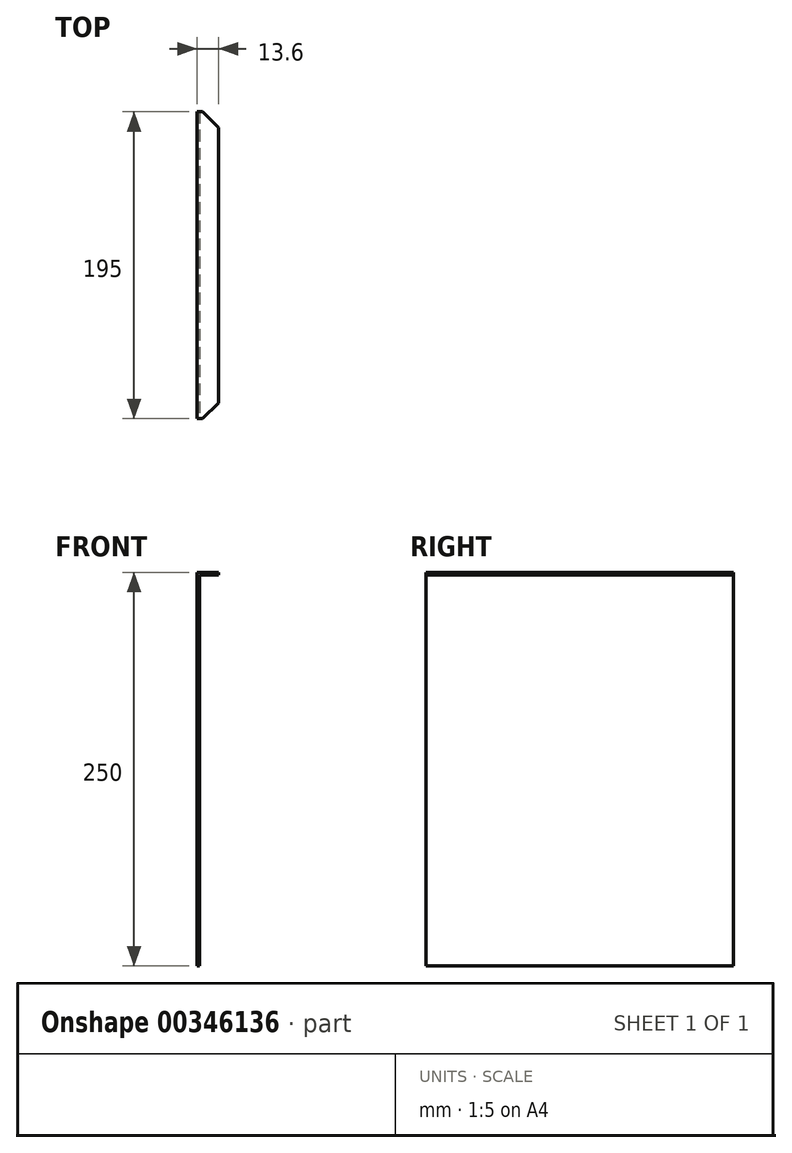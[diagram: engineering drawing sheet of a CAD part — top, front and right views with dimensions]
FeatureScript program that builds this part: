
annotation { "Feature Type Name" : "Feature", "Feature Type Description" : "" }
export const myFeature = defineFeature(function(context is Context, id is Id, definition is map)
    precondition{}
    {
        {
            var Q0;
            Q0=qCreatedBy(makeId("Right.planeOp"),FACE);
            var sketch = newSketch(context, id + "F0", { "sketchPlane" : qUnion([Q0])});
            skLineSegment(sketch, "E0.bottom", {"start": v(97.5, -125) * mm, "end": v(-97.5, -125) * mm});
            skLineSegment(sketch, "E0.top", {"start": v(97.5, 125) * mm, "end": v(-97.5, 125) * mm});
            skLineSegment(sketch, "E0.left", {"start": v(97.5, -125) * mm, "end": v(97.5, 125) * mm});
            skLineSegment(sketch, "E0.right", {"start": v(-97.5, -125) * mm, "end": v(-97.5, 125) * mm});
            skPoint(sketch, "E0.middle", {"position": v(0, 0) * mm});
            skSolve(sketch);
        }
        {
            var Q0;
            Q0=makeQuery(id+"F0.imprint","IMPRINT",FACE,{"disambiguationData":[TD([[makeQuery(id+"F0.imprint","IMPRINT",EDGE,{"derivedFrom":sQuery(id+"F0.wireOp",EDGE,"E0.bottom")}),-1.0]])]});
            extrude(context, id + "F1", {"entities" : qUnion([Q0]), "depth" : 1.6 * mm});
        }
        {
            var Q0;
            Q0=makeQuery(id+"F1.opExtrude","CAP_FACE",FACE,{"disambiguationData":[OSD([sQuery(id+"F0.wireOp",EDGE,"E0.bottom"),sQuery(id+"F0.wireOp",EDGE,"E0.top"),sQuery(id+"F0.wireOp",EDGE,"E0.left"),sQuery(id+"F0.wireOp",EDGE,"E0.right")])],"isStart":false});
            var sketch = newSketch(context, id + "F2", { "sketchPlane" : qUnion([Q0])});
            skLineSegment(sketch, "E1.bottom", {"start": v(97.5, 123.4) * mm, "end": v(-97.5, 123.4) * mm});
            skLineSegment(sketch, "E1.top", {"start": v(97.5, 125) * mm, "end": v(-97.5, 125) * mm});
            skLineSegment(sketch, "E1.left", {"start": v(97.5, 123.4) * mm, "end": v(97.5, 125) * mm});
            skLineSegment(sketch, "E1.right", {"start": v(-97.5, 123.4) * mm, "end": v(-97.5, 125) * mm});
            skPoint(sketch, "E1.middle", {"position": v(0, 124.2) * mm});
            skSolve(sketch);
        }
        {
            var Q0;
            Q0=makeQuery(id+"F2.imprint","IMPRINT",FACE,{"disambiguationData":[TD([[makeQuery(id+"F2.imprint","IMPRINT",EDGE,{"derivedFrom":sQuery(id+"F2.wireOp",EDGE,"E1.bottom")}),-1.0]])]});
            extrude(context, id + "F3", {"entities" : qUnion([Q0]), "operationType" : NewBodyOperationType.ADD, "depth" : 12 * mm});
        }
        {
            var Q0;
            Q0=makeQuery(id+"F3.opExtrude","CAP_EDGE",EDGE,{"disambiguationData":[OSD([sQuery(id+"F2.wireOp",EDGE,"E1.left")])],"isStart":false});
            var Q1;
            Q1=makeQuery(id+"F3.opExtrude","CAP_EDGE",EDGE,{"disambiguationData":[OSD([sQuery(id+"F2.wireOp",EDGE,"E1.right")])],"isStart":false});
            chamfer(context, id + "F4", {"entities" : qUnion([Q0, Q1]), "width" : 10 * mm, "tangentPropagation" : true});
        }
    });
